# Revit family: Duct_Door-Acudor-Grease_Ducts-GDD_Series
name_source: partatom
category: Specialty Equipment
revit_build: Autodesk Revit 2014 (Build: 20130308_1515(x64)
units: mm (PartAtom-declared; Revit-internal decimal feet)

## types (7) — shared parameters
Assembly Code = C1020700
Default Elevation = 0"
Description = Grease Duct Doors
Finish = Stainless Steel-Acudor-20 Gauge-Satin
Installation Type = Surface Mount
Length = 1/2"
Manufacturer = Acudor
Material = Stainless Steel-Acudor-20 Gauge-Satin
Product Documentation Link = https://www.acudor.com
Product Page URL = https://www.acudor.com
Revised Date = 08/28/2018
URL = http://acudor.com

## per-type parameters (varying)
| type | Bolt Count | Bolt Spacing | First Offset | Height | Place Holder | Width |
| GDD 7x7 | 2 | 5" | 2 1/2" | 10" | 1 | 10" |
| GDD 7x12 | 3 | 5" | 2 1/2" | 10" | 2 | 15" |
| GDD 7x20 | 5 | 4 19/32" | 2 5/16" | 10" | 3 | 23" |
| GDD 12x12 | 4 | 3 3/4" | 1 7/8" | 15" | 4 | 15" |
| GDD 12x20 | 6 | 3 27/32" | 1 29/32" | 15" | 5 | 23" |
| GDD 16x20 | 6 | 3 27/32" | 1 29/32" | 19" | 6 | 23" |
| GDD 20x20 | 8 | 2 7/8" | 1 7/16" | 23" | 7 | 23" |

note: column(s) folded — value = type name in every type: Model

## geometry (parser evidence)
native form markers: Sweep x4
no freeform markers — native parametric forms only
